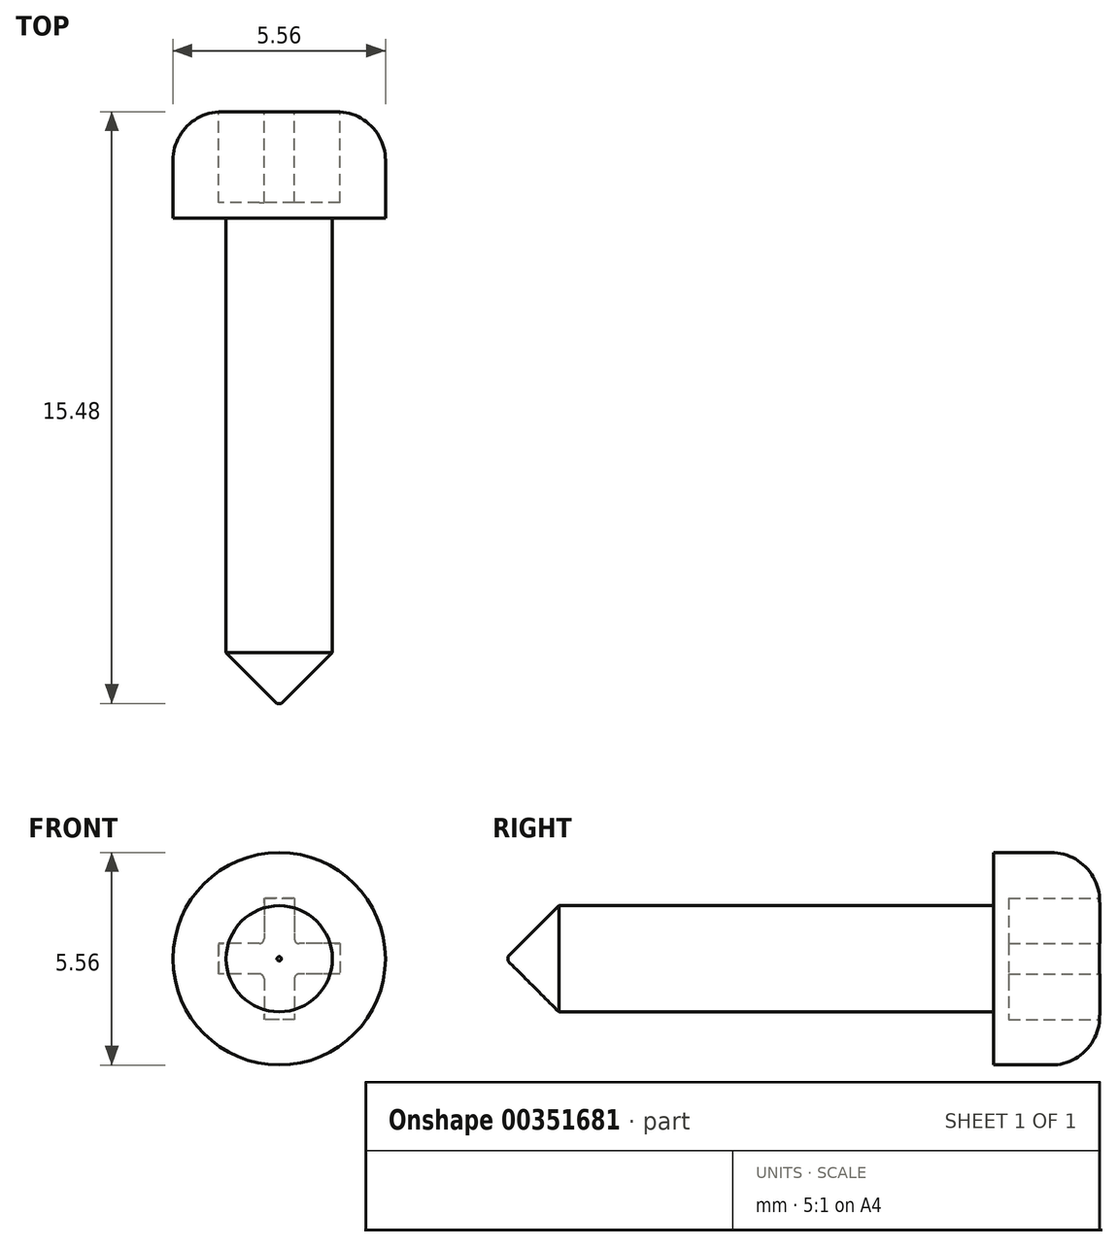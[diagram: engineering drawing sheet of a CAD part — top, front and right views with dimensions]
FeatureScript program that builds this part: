
annotation { "Feature Type Name" : "Feature", "Feature Type Description" : "" }
export const myFeature = defineFeature(function(context is Context, id is Id, definition is map)
    precondition{}
    {
        {
            var Q0;
            Q0=qCreatedBy(makeId("Front.planeOp"),FACE);
            var sketch = newSketch(context, id + "F0", { "sketchPlane" : qUnion([Q0])});
            skCircle(sketch, "E0", {"center": v(0, 0) * mm, "radius": 2.78 * mm});
            skSolve(sketch);
        }
        {
            var Q0;
            Q0 = qSketchRegion(id + "F0", true);
            extrude(context, id + "F1", {"entities" : qUnion([Q0]), "endBound" : BoundingType.SYMMETRIC, "depth" : 2.78 * mm});
        }
        {
            var Q0;
            Q0=makeQuery(id+"F1.opExtrude","CAP_FACE",FACE,{"disambiguationData":[OSD([sQuery(id+"F0.wireOp",EDGE,"E0")])],"isStart":false});
            var sketch = newSketch(context, id + "F2", { "sketchPlane" : qUnion([Q0])});
            skCircle(sketch, "E1", {"center": v(0, 0) * mm, "radius": 1.39 * mm});
            skSolve(sketch);
        }
        {
            var Q0;
            Q0 = qSketchRegion(id + "F2", true);
            extrude(context, id + "F3", {"entities" : qUnion([Q0]), "operationType" : NewBodyOperationType.ADD, "depth" : 12.7 * mm});
        }
        {
            var Q0;
            Q0=makeQuery(id+"F1.opExtrude","CAP_FACE",FACE,{"disambiguationData":[OSD([sQuery(id+"F0.wireOp",EDGE,"E0")])],"isStart":true});
            var sketch = newSketch(context, id + "F4", { "sketchPlane" : qUnion([Q0])});
            skLineSegment(sketch, "E2.bottom", {"start": v(-0.4, 1.59) * mm, "end": v(0.4, 1.59) * mm});
            skLineSegment(sketch, "E2.top", {"start": v(-0.4, -1.59) * mm, "end": v(0.4, -1.59) * mm});
            skLineSegment(sketch, "E2.left", {"start": v(-0.4, 1.59) * mm, "end": v(-0.4, -1.59) * mm});
            skLineSegment(sketch, "E2.right", {"start": v(0.4, 1.59) * mm, "end": v(0.4, -1.59) * mm});
            skPoint(sketch, "E2.middle", {"position": v(0, 0) * mm});
            skSolve(sketch);
        }
        {
            var Q0;
            Q0=makeQuery(id+"F4.imprint","IMPRINT",FACE,{"disambiguationData":[TD([[makeQuery(id+"F4.imprint","IMPRINT",EDGE,{"derivedFrom":sQuery(id+"F4.wireOp",EDGE,"E2.bottom")}),1.0]])]});
            var sketch = newSketch(context, id + "F5", { "sketchPlane" : qUnion([Q0])});
            skLineSegment(sketch, "E3.bottom", {"start": v(-1.59, 0.4) * mm, "end": v(1.59, 0.4) * mm});
            skLineSegment(sketch, "E3.top", {"start": v(-1.59, -0.4) * mm, "end": v(1.59, -0.4) * mm});
            skLineSegment(sketch, "E3.left", {"start": v(-1.59, 0.4) * mm, "end": v(-1.59, -0.4) * mm});
            skLineSegment(sketch, "E3.right", {"start": v(1.59, 0.4) * mm, "end": v(1.59, -0.4) * mm});
            skPoint(sketch, "E3.middle", {"position": v(0, 0) * mm});
            skSolve(sketch);
        }
        {
            var Q0;
            Q0 = qSketchRegion(id + "F4", true);
            extrude(context, id + "F6", {"entities" : qUnion([Q0]), "operationType" : NewBodyOperationType.REMOVE, "oppositeDirection" : true, "depth" : 2.38 * mm});
        }
        {
            var Q0;
            Q0 = qSketchRegion(id + "F5", true);
            extrude(context, id + "F7", {"entities" : qUnion([Q0]), "operationType" : NewBodyOperationType.REMOVE, "oppositeDirection" : true, "depth" : 2.38 * mm});
        }
        {
            var Q0;
            Q0=makeQuery(id+"F7.boolean.opBoolean","INTERSECT",EDGE,{"derivedFrom":[makeQuery(id+"F6.boolean.opBoolean","COPY",FACE,{"derivedFrom":makeQuery(id+"F6.opExtrude","SWEPT_FACE",FACE,{"disambiguationData":[OSD([sQuery(id+"F4.wireOp",EDGE,"E2.left")])]})}),makeQuery(id+"F7.opExtrude","SWEPT_FACE",FACE,{"disambiguationData":[OSD([sQuery(id+"F5.wireOp",EDGE,"E3.bottom")])]})]});
            var Q1;
            Q1=makeQuery(id+"F7.boolean.opBoolean","INTERSECT",EDGE,{"derivedFrom":[makeQuery(id+"F6.boolean.opBoolean","COPY",FACE,{"derivedFrom":makeQuery(id+"F6.opExtrude","SWEPT_FACE",FACE,{"disambiguationData":[OSD([sQuery(id+"F4.wireOp",EDGE,"E2.right")])]})}),makeQuery(id+"F7.opExtrude","SWEPT_FACE",FACE,{"disambiguationData":[OSD([sQuery(id+"F5.wireOp",EDGE,"E3.bottom")])]})]});
            var Q2;
            Q2=makeQuery(id+"F7.boolean.opBoolean","INTERSECT",EDGE,{"derivedFrom":[makeQuery(id+"F6.boolean.opBoolean","COPY",FACE,{"derivedFrom":makeQuery(id+"F6.opExtrude","SWEPT_FACE",FACE,{"disambiguationData":[OSD([sQuery(id+"F4.wireOp",EDGE,"E2.right")])]})}),makeQuery(id+"F7.opExtrude","SWEPT_FACE",FACE,{"disambiguationData":[OSD([sQuery(id+"F5.wireOp",EDGE,"E3.top")])]})]});
            var Q3;
            Q3=makeQuery(id+"F7.boolean.opBoolean","INTERSECT",EDGE,{"derivedFrom":[makeQuery(id+"F6.boolean.opBoolean","COPY",FACE,{"derivedFrom":makeQuery(id+"F6.opExtrude","SWEPT_FACE",FACE,{"disambiguationData":[OSD([sQuery(id+"F4.wireOp",EDGE,"E2.left")])]})}),makeQuery(id+"F7.opExtrude","SWEPT_FACE",FACE,{"disambiguationData":[OSD([sQuery(id+"F5.wireOp",EDGE,"E3.top")])]})]});
            fillet(context, id + "F8", {"entities" : qUnion([Q0, Q1, Q2, Q3]), "radius" : 0.13 * mm, "tangentPropagation" : true, "allowEdgeOverflow" : false});
        }
        {
            var Q0;
            Q0=makeQuery(id+"F1.opExtrude","CAP_EDGE",EDGE,{"disambiguationData":[OSD([sQuery(id+"F0.wireOp",EDGE,"E0")])],"isStart":true});
            fillet(context, id + "F9", {"entities" : qUnion([Q0]), "radius" : 1.27 * mm, "tangentPropagation" : true, "allowEdgeOverflow" : false});
        }
        {
            var Q0;
            Q0=makeQuery(id+"F3.opExtrude","CAP_EDGE",EDGE,{"disambiguationData":[OSD([sQuery(id+"F2.wireOp",EDGE,"E1")])],"isStart":false});
            chamfer(context, id + "F10", {"entities" : qUnion([Q0]), "width" : 1.33 * mm, "tangentPropagation" : true});
        }
    });
